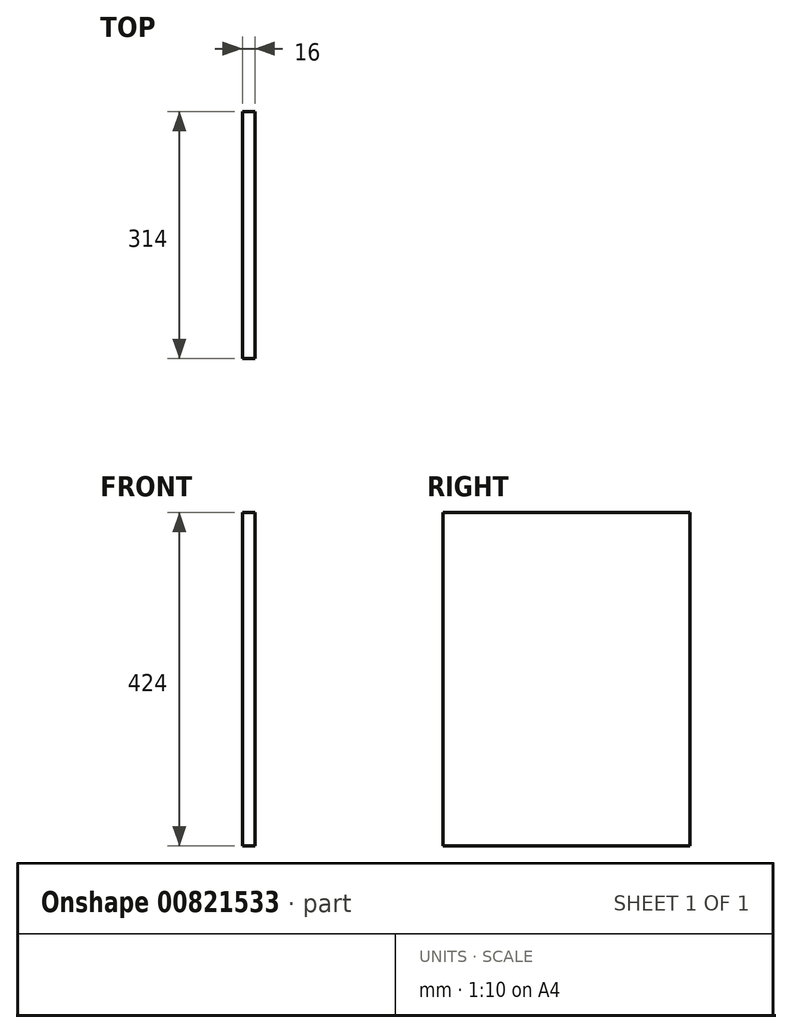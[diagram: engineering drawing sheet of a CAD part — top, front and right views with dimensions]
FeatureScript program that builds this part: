
annotation { "Feature Type Name" : "Feature", "Feature Type Description" : "" }
export const myFeature = defineFeature(function(context is Context, id is Id, definition is map)
    precondition{}
    {
        {
            var Q0;
            Q0=qCreatedBy(makeId("Right.planeOp"),FACE);
            var sketch = newSketch(context, id + "F0", { "sketchPlane" : qUnion([Q0])});
            skLineSegment(sketch, "E0.bottom", {"start": v(-157, 212) * mm, "end": v(157, 212) * mm});
            skLineSegment(sketch, "E0.top", {"start": v(-157, -212) * mm, "end": v(157, -212) * mm});
            skLineSegment(sketch, "E0.left", {"start": v(-157, 212) * mm, "end": v(-157, -212) * mm});
            skLineSegment(sketch, "E0.right", {"start": v(157, 212) * mm, "end": v(157, -212) * mm});
            skPoint(sketch, "E0.middle", {"position": v(0, 0) * mm});
            skSolve(sketch);
        }
        {
            var Q0;
            Q0=makeQuery(id+"F0.imprint","IMPRINT",FACE,{"disambiguationData":[TD([[makeQuery(id+"F0.imprint","IMPRINT",EDGE,{"derivedFrom":sQuery(id+"F0.wireOp",EDGE,"E0.bottom")}),-1.0]])]});
            extrude(context, id + "F1", {"entities" : qUnion([Q0]), "endBound" : BoundingType.SYMMETRIC, "depth" : 16 * mm, "offsetDistance" : 25 * mm});
        }
    });
